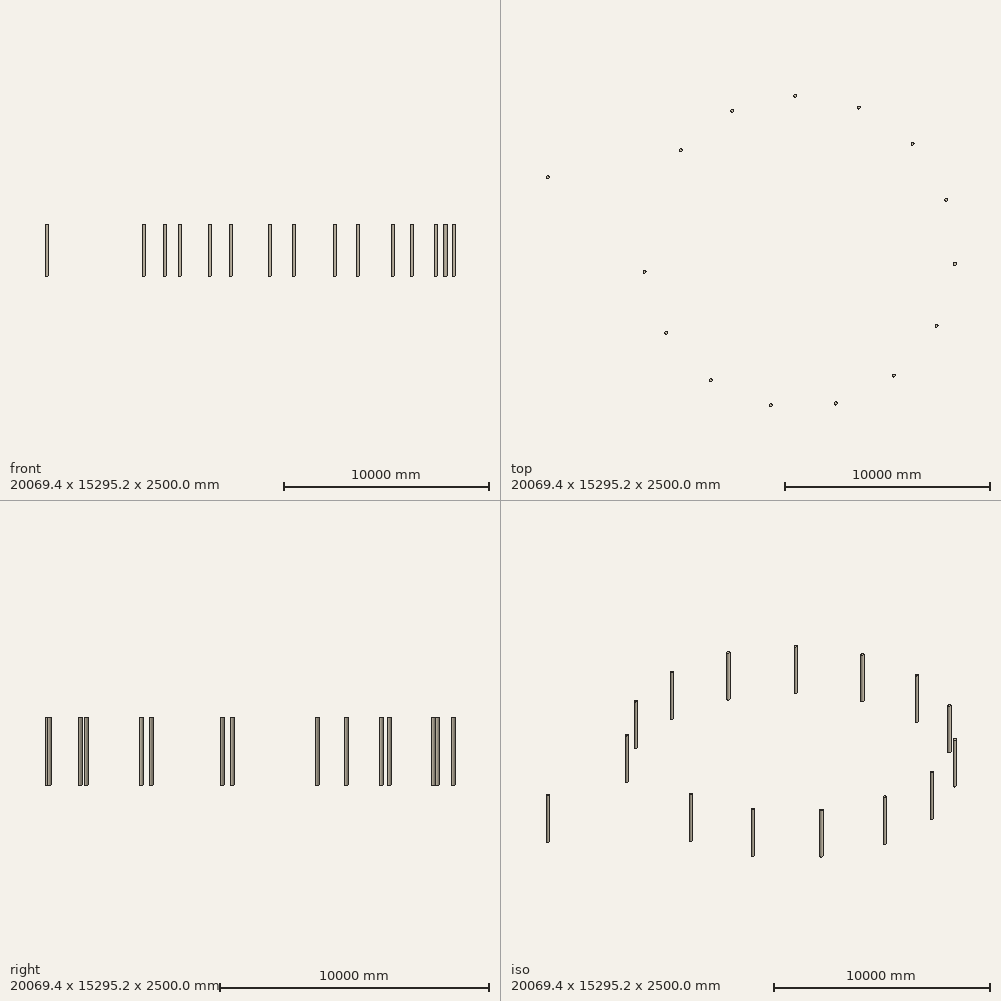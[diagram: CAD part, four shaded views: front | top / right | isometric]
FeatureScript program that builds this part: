
annotation { "Feature Type Name" : "Feature", "Feature Type Description" : "" }
export const myFeature = defineFeature(function(context is Context, id is Id, definition is map)
    precondition{}
    {
        {
            var Q0;
            Q0=qCreatedBy(makeId("Top.planeOp"),FACE);
            var sketch = newSketch(context, id + "F0", { "sketchPlane" : qUnion([Q0])});
            skCircle(sketch, "E0", {"center": v(-12305.11, 3644.58) * mm, "radius": 36.99 * mm});
            skCircle(sketch, "E1", {"center": v(-12305.11, 3644.58) * mm, "radius": 75 * mm});
            skCircle(sketch, "E2.1.0", {"center": v(-7572.48, -997.14) * mm, "radius": 75 * mm});
            skCircle(sketch, "E2.2.0", {"center": v(-6512.23, -3990.94) * mm, "radius": 75 * mm});
            skCircle(sketch, "E3.1.3.0", {"center": v(-4325.96, -6294.67) * mm, "radius": 75 * mm});
            skCircle(sketch, "E3.1.4.0", {"center": v(-1391.68, -7510) * mm, "radius": 75 * mm});
            skCircle(sketch, "E3.1.5.0", {"center": v(1783.22, -7426.77) * mm, "radius": 75 * mm});
            skCircle(sketch, "E3.1.6.0", {"center": v(4649.8, -6059.39) * mm, "radius": 75 * mm});
            skCircle(sketch, "E3.1.7.0", {"center": v(6712.37, -3644.29) * mm, "radius": 75 * mm});
            skCircle(sketch, "E3.1.8.0", {"center": v(7614.32, -599.05) * mm, "radius": 75 * mm});
            skCircle(sketch, "E3.1.9.0", {"center": v(7199.69, 2549.76) * mm, "radius": 75 * mm});
            skCircle(sketch, "E3.1.10.0", {"center": v(5540.16, 5257.7) * mm, "radius": 75 * mm});
            skCircle(sketch, "E3.1.11.0", {"center": v(2922.69, 7056.53) * mm, "radius": 75 * mm});
            skCircle(sketch, "E3.1.12.0", {"center": v(-200.14, 7635.23) * mm, "radius": 75 * mm});
            skCircle(sketch, "E3.1.13.0", {"center": v(-3288.37, 6893.72) * mm, "radius": 75 * mm});
            skCircle(sketch, "E3.1.14.0", {"center": v(-5808, 4960.23) * mm, "radius": 75 * mm});
            skSolve(sketch);
        }
        {
            var Q0;
            Q0=makeQuery(id+"F0.imprint","IMPRINT",FACE,{"disambiguationData":[TD([[makeQuery(id+"F0.imprint","IMPRINT",EDGE,{"derivedFrom":sQuery(id+"F0.wireOp",EDGE,"E3.1.4.0")}),1.0]])]});
            var Q1;
            Q1=makeQuery(id+"F0.imprint","IMPRINT",FACE,{"disambiguationData":[TD([[makeQuery(id+"F0.imprint","IMPRINT",EDGE,{"derivedFrom":sQuery(id+"F0.wireOp",EDGE,"E3.1.5.0")}),1.0]])]});
            var Q2;
            Q2=makeQuery(id+"F0.imprint","IMPRINT",FACE,{"disambiguationData":[TD([[makeQuery(id+"F0.imprint","IMPRINT",EDGE,{"derivedFrom":sQuery(id+"F0.wireOp",EDGE,"E3.1.6.0")}),1.0]])]});
            var Q3;
            Q3=makeQuery(id+"F0.imprint","IMPRINT",FACE,{"disambiguationData":[TD([[makeQuery(id+"F0.imprint","IMPRINT",EDGE,{"derivedFrom":sQuery(id+"F0.wireOp",EDGE,"E3.1.7.0")}),1.0]])]});
            var Q4;
            Q4=makeQuery(id+"F0.imprint","IMPRINT",FACE,{"disambiguationData":[TD([[makeQuery(id+"F0.imprint","IMPRINT",EDGE,{"derivedFrom":sQuery(id+"F0.wireOp",EDGE,"E3.1.8.0")}),1.0]])]});
            var Q5;
            Q5=makeQuery(id+"F0.imprint","IMPRINT",FACE,{"disambiguationData":[TD([[makeQuery(id+"F0.imprint","IMPRINT",EDGE,{"derivedFrom":sQuery(id+"F0.wireOp",EDGE,"E3.1.9.0")}),1.0]])]});
            var Q6;
            Q6=makeQuery(id+"F0.imprint","IMPRINT",FACE,{"disambiguationData":[TD([[makeQuery(id+"F0.imprint","IMPRINT",EDGE,{"derivedFrom":sQuery(id+"F0.wireOp",EDGE,"E3.1.10.0")}),1.0]])]});
            var Q7;
            Q7=makeQuery(id+"F0.imprint","IMPRINT",FACE,{"disambiguationData":[TD([[makeQuery(id+"F0.imprint","IMPRINT",EDGE,{"derivedFrom":sQuery(id+"F0.wireOp",EDGE,"E3.1.11.0")}),1.0]])]});
            var Q8;
            Q8=makeQuery(id+"F0.imprint","IMPRINT",FACE,{"disambiguationData":[TD([[makeQuery(id+"F0.imprint","IMPRINT",EDGE,{"derivedFrom":sQuery(id+"F0.wireOp",EDGE,"E3.1.12.0")}),1.0]])]});
            var Q9;
            Q9=makeQuery(id+"F0.imprint","IMPRINT",FACE,{"disambiguationData":[TD([[makeQuery(id+"F0.imprint","IMPRINT",EDGE,{"derivedFrom":sQuery(id+"F0.wireOp",EDGE,"E3.1.13.0")}),1.0]])]});
            var Q10;
            Q10=makeQuery(id+"F0.imprint","IMPRINT",FACE,{"disambiguationData":[TD([[makeQuery(id+"F0.imprint","IMPRINT",EDGE,{"derivedFrom":sQuery(id+"F0.wireOp",EDGE,"E3.1.14.0")}),1.0]])]});
            var Q11;
            Q11=makeQuery(id+"F0.imprint","IMPRINT",FACE,{"disambiguationData":[TD([[makeQuery(id+"F0.imprint","IMPRINT",EDGE,{"derivedFrom":sQuery(id+"F0.wireOp",EDGE,"E2.2.0")}),1.0]])]});
            var Q12;
            Q12=makeQuery(id+"F0.imprint","IMPRINT",FACE,{"disambiguationData":[TD([[makeQuery(id+"F0.imprint","IMPRINT",EDGE,{"derivedFrom":sQuery(id+"F0.wireOp",EDGE,"E2.1.0")}),1.0]])]});
            var Q13;
            Q13=makeQuery(id+"F0.imprint","IMPRINT",FACE,{"disambiguationData":[TD([[makeQuery(id+"F0.imprint","IMPRINT",EDGE,{"derivedFrom":sQuery(id+"F0.wireOp",EDGE,"E3.1.3.0")}),1.0]])]});
            var Q14;
            Q14=makeQuery(id+"F0.imprint","IMPRINT",FACE,{"disambiguationData":[TD([[makeQuery(id+"F0.imprint","IMPRINT",EDGE,{"derivedFrom":sQuery(id+"F0.wireOp",EDGE,"E0")}),-1.0]])]});
            var Q15;
            Q15=makeQuery(id+"F0.imprint","IMPRINT",FACE,{"disambiguationData":[TD([[makeQuery(id+"F0.imprint","IMPRINT",EDGE,{"derivedFrom":sQuery(id+"F0.wireOp",EDGE,"E0")}),1.0]])]});
            extrude(context, id + "F1", {"entities" : qUnion([Q0, Q1, Q2, Q3, Q4, Q5, Q6, Q7, Q8, Q9, Q10, Q11, Q12, Q13, Q14, Q15]), "depth" : 2500 * mm});
        }
    });
